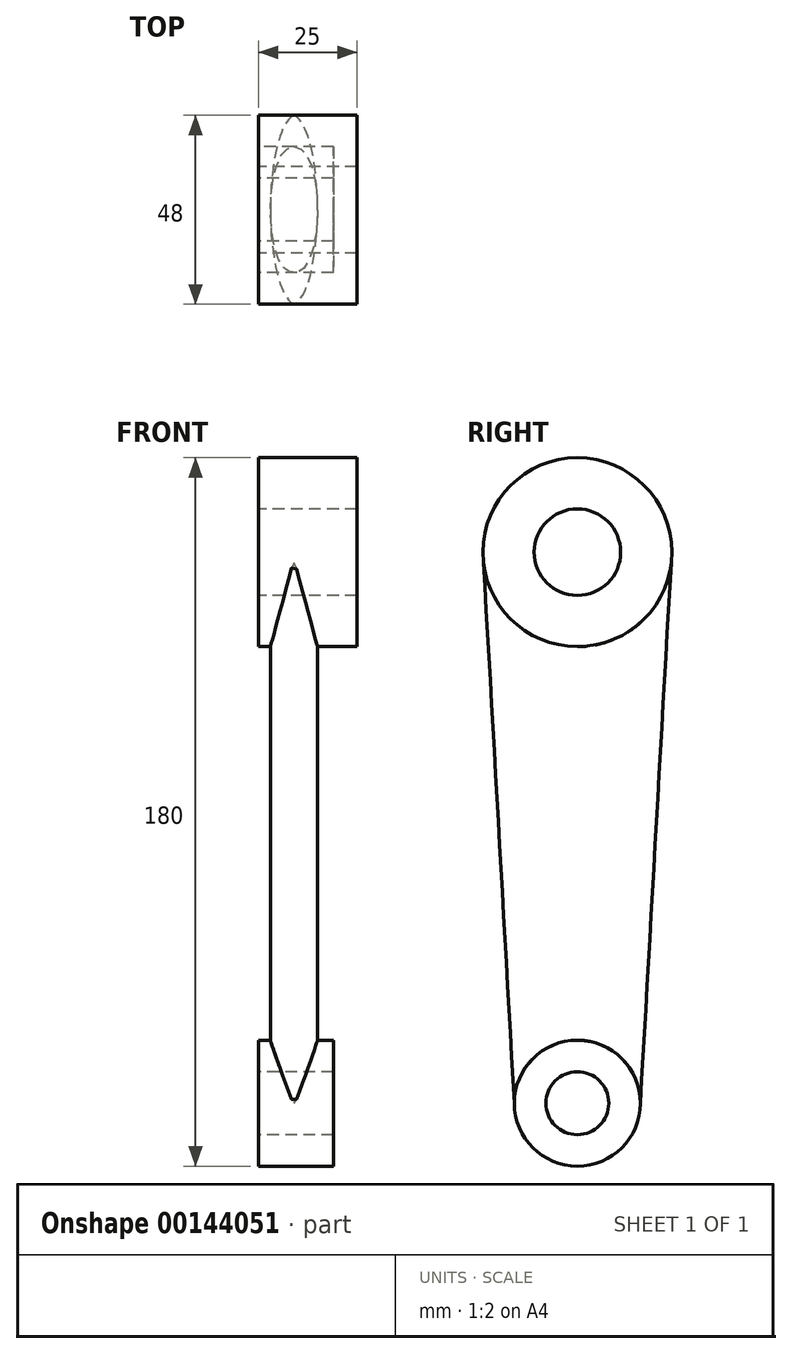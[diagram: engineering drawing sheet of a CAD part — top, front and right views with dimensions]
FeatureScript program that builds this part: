
annotation { "Feature Type Name" : "Feature", "Feature Type Description" : "" }
export const myFeature = defineFeature(function(context is Context, id is Id, definition is map)
    precondition{}
    {
        {
            var Q0;
            Q0=qCreatedBy(makeId("Right.planeOp"),FACE);
            var sketch = newSketch(context, id + "F0", { "sketchPlane" : qUnion([Q0])});
            skCircle(sketch, "E0", {"center": v(0, 0) * mm, "radius": 8 * mm});
            skCircle(sketch, "E1", {"center": v(0, 0) * mm, "radius": 16 * mm});
            skCircle(sketch, "E2", {"center": v(0, 140) * mm, "radius": 11 * mm});
            skCircle(sketch, "E3", {"center": v(0, 140) * mm, "radius": 24 * mm});
            skSolve(sketch);
        }
        {
            var Q0;
            Q0=makeQuery(id+"F0.imprint","IMPRINT",FACE,{"disambiguationData":[TD([[makeQuery(id+"F0.imprint","IMPRINT",EDGE,{"derivedFrom":sQuery(id+"F0.wireOp",EDGE,"E0")}),-1.0]])]});
            var Q1;
            Q1=makeQuery(id+"F0.imprint","IMPRINT",FACE,{"disambiguationData":[TD([[makeQuery(id+"F0.imprint","IMPRINT",EDGE,{"derivedFrom":sQuery(id+"F0.wireOp",EDGE,"E0")}),1.0]])]});
            extrude(context, id + "F1", {"entities" : qUnion([Q0, Q1]), "depth" : 19 * mm});
        }
        {
            var Q0;
            Q0=makeQuery(id+"F0.imprint","IMPRINT",FACE,{"disambiguationData":[TD([[makeQuery(id+"F0.imprint","IMPRINT",EDGE,{"derivedFrom":sQuery(id+"F0.wireOp",EDGE,"E2")}),-1.0]])]});
            var Q1;
            Q1=makeQuery(id+"F0.imprint","IMPRINT",FACE,{"disambiguationData":[TD([[makeQuery(id+"F0.imprint","IMPRINT",EDGE,{"derivedFrom":sQuery(id+"F0.wireOp",EDGE,"E2")}),1.0]])]});
            extrude(context, id + "F2", {"entities" : qUnion([Q0, Q1]), "depth" : 25 * mm});
        }
        {
            var Q0;
            Q0=qCreatedBy(makeId("Top.planeOp"),FACE);
            var sketch = newSketch(context, id + "F3", { "sketchPlane" : qUnion([Q0])});
            skEllipse(sketch, "E4", {"center": v(9, 0) * mm, "majorRadius": 16 * mm, "minorRadius": 6 * mm, "majorAxis": v(0, 1)});
            skPoint(sketch, "E5", {"position": v(3, 0) * mm});
            skLineSegment(sketch, "E6", {"start": v(0, 16) * mm, "end": v(19, 16) * mm, "construction": true});
            skSolve(sketch);
        }
        {
            var Q0;
            Q0=sQuery(id+"F0.wireOp",VERTEX,"E3.center");
            var Q1;
            Q1=qCreatedBy(makeId("Top.planeOp"),FACE);
            cPlane(context, id + "F4", {"entities" : qUnion([Q0, Q1]), "cplaneType" : CPlaneType.PLANE_POINT, "offset" : 25 * mm, "width" : 150 * mm, "height" : 150 * mm});
        }
        {
            var Q0;
            Q0=qCreatedBy(id+"F4.planeOp",FACE);
            var sketch = newSketch(context, id + "F5", { "sketchPlane" : qUnion([Q0])});
            skEllipse(sketch, "E7", {"center": v(9, 0) * mm, "majorRadius": 24 * mm, "minorRadius": 6 * mm, "majorAxis": v(0, 1)});
            skLineSegment(sketch, "E8", {"start": v(0, 24) * mm, "end": v(25, 24) * mm, "construction": true});
            skPoint(sketch, "E9", {"position": v(3, 0) * mm});
            skSolve(sketch);
        }
        {
            var Q0;
            Q0=makeQuery(id+"F5.imprint","IMPRINT",FACE,{"disambiguationData":[TD([[makeQuery(id+"F5.imprint","IMPRINT",EDGE,{"derivedFrom":sQuery(id+"F5.wireOp",EDGE,"E7")}),1.0]])]});
            var Q1;
            Q1=makeQuery(id+"F3.imprint","IMPRINT",FACE,{"disambiguationData":[TD([[makeQuery(id+"F3.imprint","IMPRINT",EDGE,{"derivedFrom":sQuery(id+"F3.wireOp",EDGE,"E4")}),1.0]])]});
            loft(context, id + "F6", {"operationType" : NewBodyOperationType.ADD, "sheetProfilesArray" : [{ "sheetProfileEntities" : qUnion([Q0]) }, { "sheetProfileEntities" : qUnion([Q1]) }]});
        }
        {
            var Q0;
            Q0=makeQuery(id+"F0.imprint","IMPRINT",FACE,{"disambiguationData":[TD([[makeQuery(id+"F0.imprint","IMPRINT",EDGE,{"derivedFrom":sQuery(id+"F0.wireOp",EDGE,"E2")}),1.0]])]});
            var Q1;
            Q1=makeQuery(id+"F0.imprint","IMPRINT",FACE,{"disambiguationData":[TD([[makeQuery(id+"F0.imprint","IMPRINT",EDGE,{"derivedFrom":sQuery(id+"F0.wireOp",EDGE,"E0")}),1.0]])]});
            var Q2;
            Q2=sQuery(id+"F0.wireOp",EDGE,"E2");
            var Q3;
            Q3=sQuery(id+"F0.wireOp",EDGE,"E0");
            extrude(context, id + "F7", {"entities" : qUnion([Q0, Q1]), "operationType" : NewBodyOperationType.REMOVE, "surfaceEntities" : qUnion([Q2, Q3]), "endBound" : BoundingType.THROUGH_ALL, "depth" : 25 * mm});
        }
    });
